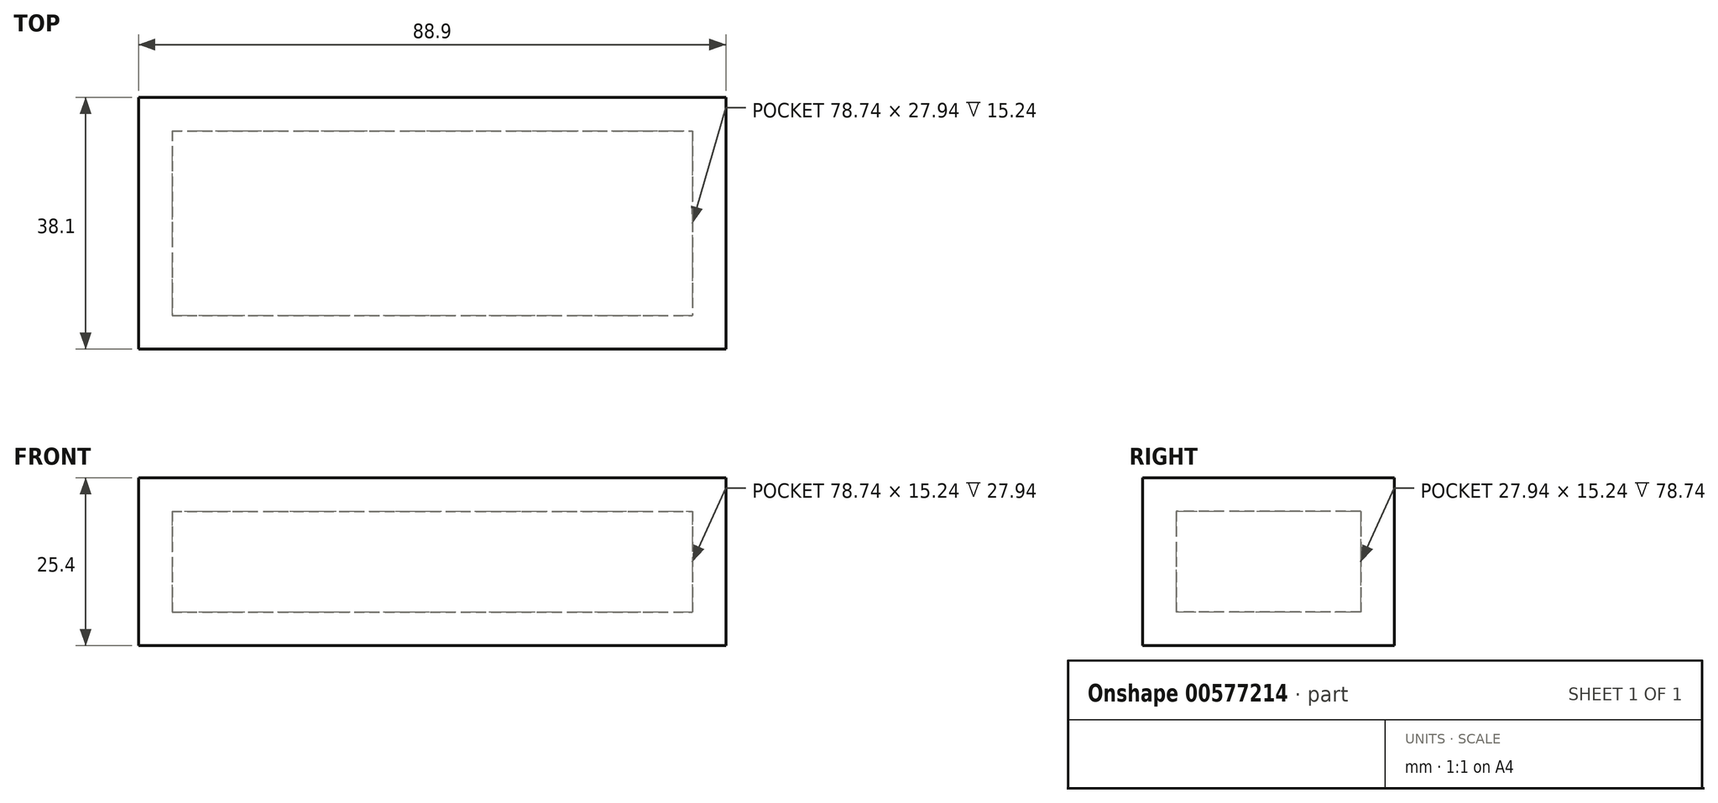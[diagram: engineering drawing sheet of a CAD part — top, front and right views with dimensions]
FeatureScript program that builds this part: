
annotation { "Feature Type Name" : "Feature", "Feature Type Description" : "" }
export const myFeature = defineFeature(function(context is Context, id is Id, definition is map)
    precondition{}
    {
        {
            var Q0;
            Q0=qCreatedBy(makeId("Top.planeOp"),FACE);
            var sketch = newSketch(context, id + "F0", { "sketchPlane" : qUnion([Q0])});
            skLineSegment(sketch, "E0.bottom", {"start": v(-36.7, 61.72) * mm, "end": v(52.2, 61.72) * mm});
            skLineSegment(sketch, "E0.top", {"start": v(-36.7, 23.62) * mm, "end": v(52.2, 23.62) * mm});
            skLineSegment(sketch, "E0.left", {"start": v(-36.7, 61.72) * mm, "end": v(-36.7, 23.62) * mm});
            skLineSegment(sketch, "E0.right", {"start": v(52.2, 61.72) * mm, "end": v(52.2, 23.62) * mm});
            skSolve(sketch);
        }
        {
            var Q0;
            Q0=makeQuery(id+"F0.imprint","IMPRINT",FACE,{"disambiguationData":[TD([[makeQuery(id+"F0.imprint","IMPRINT",EDGE,{"derivedFrom":sQuery(id+"F0.wireOp",EDGE,"E0.bottom")}),-1.0]])]});
            extrude(context, id + "F1", {"entities" : qUnion([Q0]), "depth" : 25.4 * mm, "offsetDistance" : 25.4 * mm});
        }
        {
            var Q0;
            Q0=makeQuery(id+"F1.opExtrude","SWEPT_FACE",FACE,{"disambiguationData":[OSD([sQuery(id+"F0.wireOp",EDGE,"E0.right")])]});
            var Q1;
            Q1=makeQuery(id+"F1.opExtrude","SWEPT_BODY",BODY,{"disambiguationData":[OSD([sQuery(id+"F0.wireOp",EDGE,"E0.bottom"),sQuery(id+"F0.wireOp",EDGE,"E0.top"),sQuery(id+"F0.wireOp",EDGE,"E0.left"),sQuery(id+"F0.wireOp",EDGE,"E0.right")])]});
            shell(context, id + "F2", {"isHollow" : true, "entities" : qUnion([Q0]), "parts" : qUnion([Q1]), "thickness" : 5.08 * mm});
        }
    });
